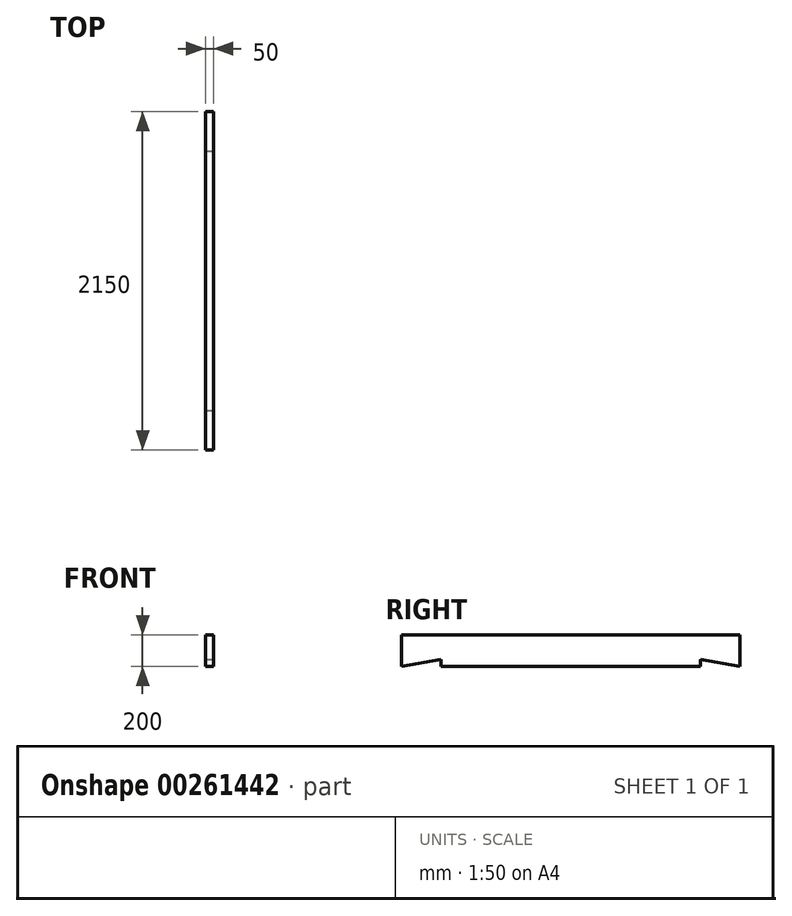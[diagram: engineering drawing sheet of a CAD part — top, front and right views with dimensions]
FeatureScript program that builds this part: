
annotation { "Feature Type Name" : "Feature", "Feature Type Description" : "" }
export const myFeature = defineFeature(function(context is Context, id is Id, definition is map)
    precondition{}
    {
        {
            var Q0;
            Q0=qCreatedBy(makeId("Front.planeOp"),FACE);
            var sketch = newSketch(context, id + "F0", { "sketchPlane" : qUnion([Q0])});
            skLineSegment(sketch, "E0.bottom", {"start": v(25, -100) * mm, "end": v(-25, -100) * mm});
            skLineSegment(sketch, "E0.top", {"start": v(25, 100) * mm, "end": v(-25, 100) * mm});
            skLineSegment(sketch, "E0.left", {"start": v(25, -100) * mm, "end": v(25, 100) * mm});
            skLineSegment(sketch, "E0.right", {"start": v(-25, -100) * mm, "end": v(-25, 100) * mm});
            skPoint(sketch, "E0.middle", {"position": v(0, 0) * mm});
            skSolve(sketch);
        }
        {
            var Q0;
            Q0=makeQuery(id+"F0.imprint","IMPRINT",FACE,{"disambiguationData":[TD([[makeQuery(id+"F0.imprint","IMPRINT",EDGE,{"derivedFrom":sQuery(id+"F0.wireOp",EDGE,"E0.bottom")}),-1.0]])]});
            extrude(context, id + "F1", {"entities" : qUnion([Q0]), "depth" : 2150 * mm});
        }
        {
            var Q0;
            Q0=makeQuery(id+"F1.opExtrude","SWEPT_FACE",FACE,{"disambiguationData":[OSD([sQuery(id+"F0.wireOp",EDGE,"E0.left")])]});
            var sketch = newSketch(context, id + "F2", { "sketchPlane" : qUnion([Q0])});
            skSolve(sketch);
        }
        {
            var Q0;
            {var subQ0=sQuery(id+"F0.wireOp",EDGE,"E0.left");Q0=makeQuery(id+"F2.imprint","IMPRINT",FACE,{"disambiguationData":[TD([[makeQuery(id+"F2.imprint","IMPRINT",EDGE,{"derivedFrom":makeQuery(id+"F1.opExtrude","CAP_EDGE",EDGE,{"disambiguationData":[OSD([subQ0])],"isStart":true})}),1.0]])]});}
            var sketch = newSketch(context, id + "F3", { "sketchPlane" : qUnion([Q0])});
            skLineSegment(sketch, "E1", {"start": v(-1900, -55.92) * mm, "end": v(-1900, -100) * mm});
            skLineSegment(sketch, "E2.0.0", {"start": v(-2150, -100) * mm, "end": v(0, -100) * mm});
            skLineSegment(sketch, "E2.0.1", {"start": v(0, -100) * mm, "end": v(0, 100) * mm});
            skLineSegment(sketch, "E2.0.2", {"start": v(0, 100) * mm, "end": v(-1900, 100) * mm});
            skLineSegment(sketch, "E3", {"start": v(-2150, -100) * mm, "end": v(-1900, -55.92) * mm});
            skPoint(sketch, "E4.orphan", {"position": v(-2150, 100) * mm});
            skSolve(sketch);
        }
        {
            var Q0;
            {var subQ0=sQuery(id+"F3.wireOp",EDGE,"E1");Q0=makeQuery(id+"F3.imprint","IMPRINT",FACE,{"disambiguationData":[TD([[makeQuery(id+"F3.imprint","IMPRINT",EDGE,{"derivedFrom":subQ0}),-1.0]])]});}
            extrude(context, id + "F4", {"entities" : qUnion([Q0]), "operationType" : NewBodyOperationType.REMOVE, "oppositeDirection" : true, "depth" : 50 * mm});
        }
        {
            var Q0;
            {var subQ0=sQuery(id+"F0.wireOp",EDGE,"E0.left");Q0=makeQuery(id+"F2.imprint","IMPRINT",FACE,{"disambiguationData":[TD([[makeQuery(id+"F2.imprint","IMPRINT",EDGE,{"derivedFrom":makeQuery(id+"F1.opExtrude","CAP_EDGE",EDGE,{"disambiguationData":[OSD([subQ0])],"isStart":true})}),1.0]])]});}
            var sketch = newSketch(context, id + "F5", { "sketchPlane" : qUnion([Q0])});
            skLineSegment(sketch, "E5.0.0", {"start": v(-2150, -100) * mm, "end": v(0, -100) * mm});
            skLineSegment(sketch, "E5.0.1", {"start": v(0, -100) * mm, "end": v(0, 100) * mm});
            skLineSegment(sketch, "E5.0.2", {"start": v(0, 100) * mm, "end": v(-2150, 100) * mm});
            skLineSegment(sketch, "E5.0.3", {"start": v(-2150, 100) * mm, "end": v(-2150, -100) * mm});
            skLineSegment(sketch, "E6", {"start": v(-250, -100) * mm, "end": v(-250, -55.92) * mm});
            skLineSegment(sketch, "E7", {"start": v(0, -100) * mm, "end": v(-250, -55.92) * mm});
            skSolve(sketch);
        }
        {
            var Q0;
            {var subQ2=sQuery(id+"F5.wireOp",EDGE,"E6");Q0=makeQuery(id+"F5.imprint","IMPRINT",FACE,{"disambiguationData":[TD([[makeQuery(id+"F5.imprint","IMPRINT",EDGE,{"derivedFrom":subQ2}),-1.0]])]});}
            extrude(context, id + "F6", {"entities" : qUnion([Q0]), "operationType" : NewBodyOperationType.REMOVE, "oppositeDirection" : true, "depth" : 50 * mm});
        }
    });
